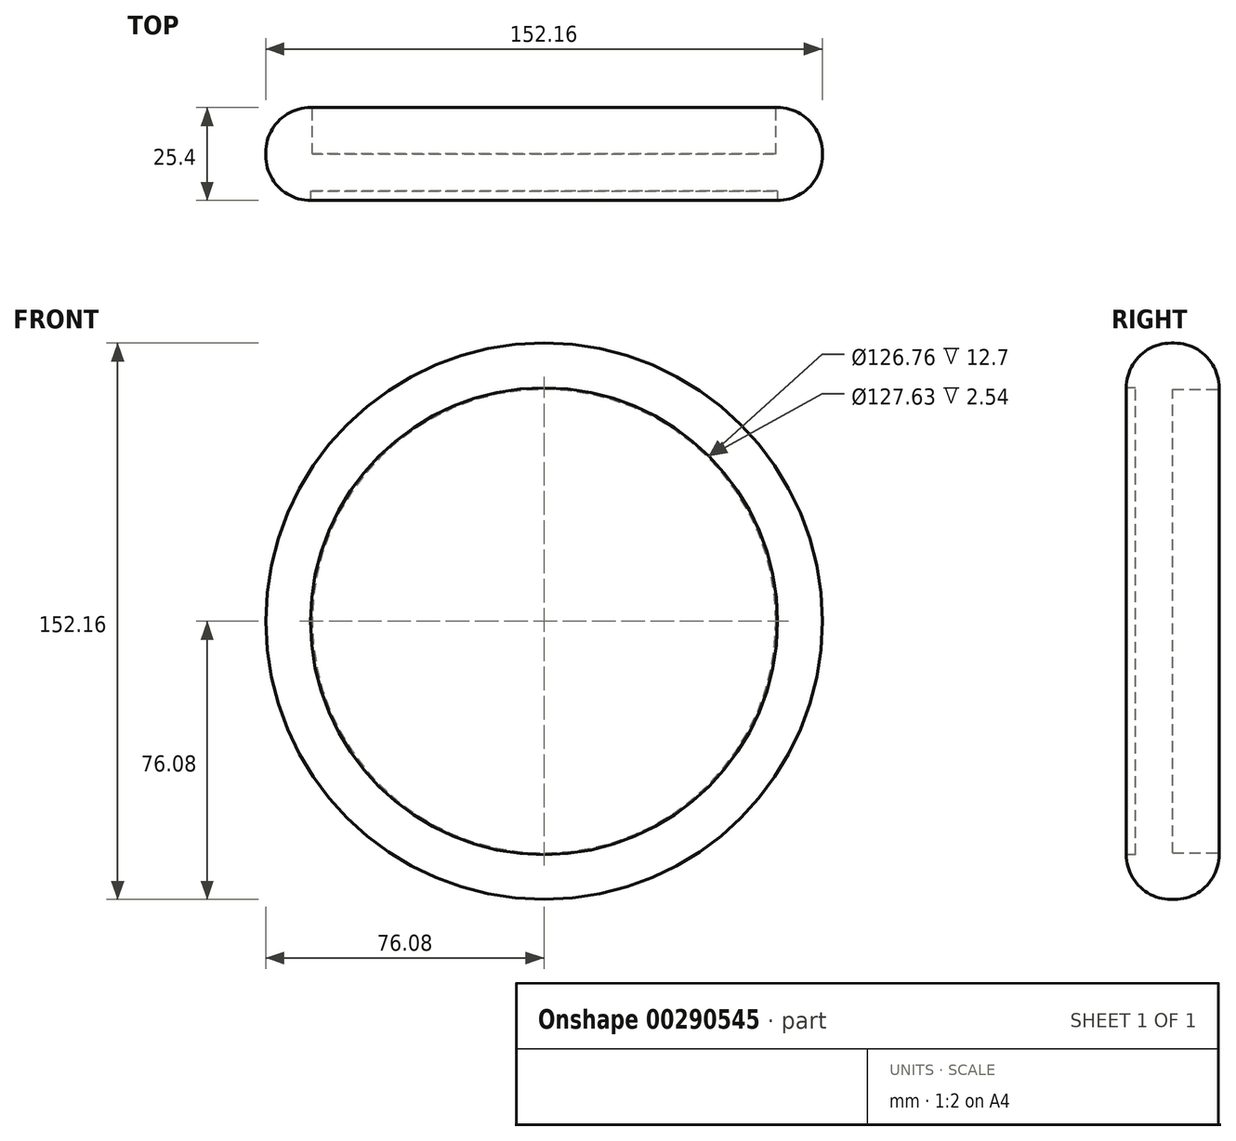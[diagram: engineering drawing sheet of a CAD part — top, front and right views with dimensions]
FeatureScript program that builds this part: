
annotation { "Feature Type Name" : "Feature", "Feature Type Description" : "" }
export const myFeature = defineFeature(function(context is Context, id is Id, definition is map)
    precondition{}
    {
        {
            var Q0;
            Q0=qCreatedBy(makeId("Front.planeOp"),FACE);
            var sketch = newSketch(context, id + "F0", { "sketchPlane" : qUnion([Q0])});
            skCircle(sketch, "E0", {"center": v(0, 0) * mm, "radius": 76.08 * mm});
            skSolve(sketch);
        }
        {
            var Q0;
            Q0=makeQuery(id+"F0.imprint","IMPRINT",FACE,{"disambiguationData":[TD([[makeQuery(id+"F0.imprint","IMPRINT",EDGE,{"derivedFrom":sQuery(id+"F0.wireOp",EDGE,"E0")}),1.0]])]});
            extrude(context, id + "F1", {"entities" : qUnion([Q0]), "depth" : 25.4 * mm});
        }
        {
            var Q0;
            Q0=makeQuery(id+"F1.opExtrude","CAP_EDGE",EDGE,{"disambiguationData":[OSD([sQuery(id+"F0.wireOp",EDGE,"E0")])],"isStart":false});
            var Q1;
            Q1=makeQuery(id+"F1.opExtrude","SWEPT_FACE",FACE,{"disambiguationData":[OSD([sQuery(id+"F0.wireOp",EDGE,"E0")])]});
            fillet(context, id + "F2", {"entities" : qUnion([Q0, Q1]), "radius" : 12.26 * mm, "tangentPropagation" : true, "allowEdgeOverflow" : false});
        }
        {
            var Q0;
            Q0=makeQuery(id+"F1.opExtrude","CAP_FACE",FACE,{"disambiguationData":[OSD([sQuery(id+"F0.wireOp",EDGE,"E0")])],"isStart":true});
            shell(context, id + "F3", {"entities" : qUnion([Q0]), "thickness" : 12.7 * mm});
        }
        {
            var Q0;
            Q0=makeQuery(id+"F1.opExtrude","CAP_FACE",FACE,{"disambiguationData":[OSD([sQuery(id+"F0.wireOp",EDGE,"E0")])],"isStart":false});
            shell(context, id + "F4", {"entities" : qUnion([Q0]), "thickness" : 10.16 * mm});
        }
    });
